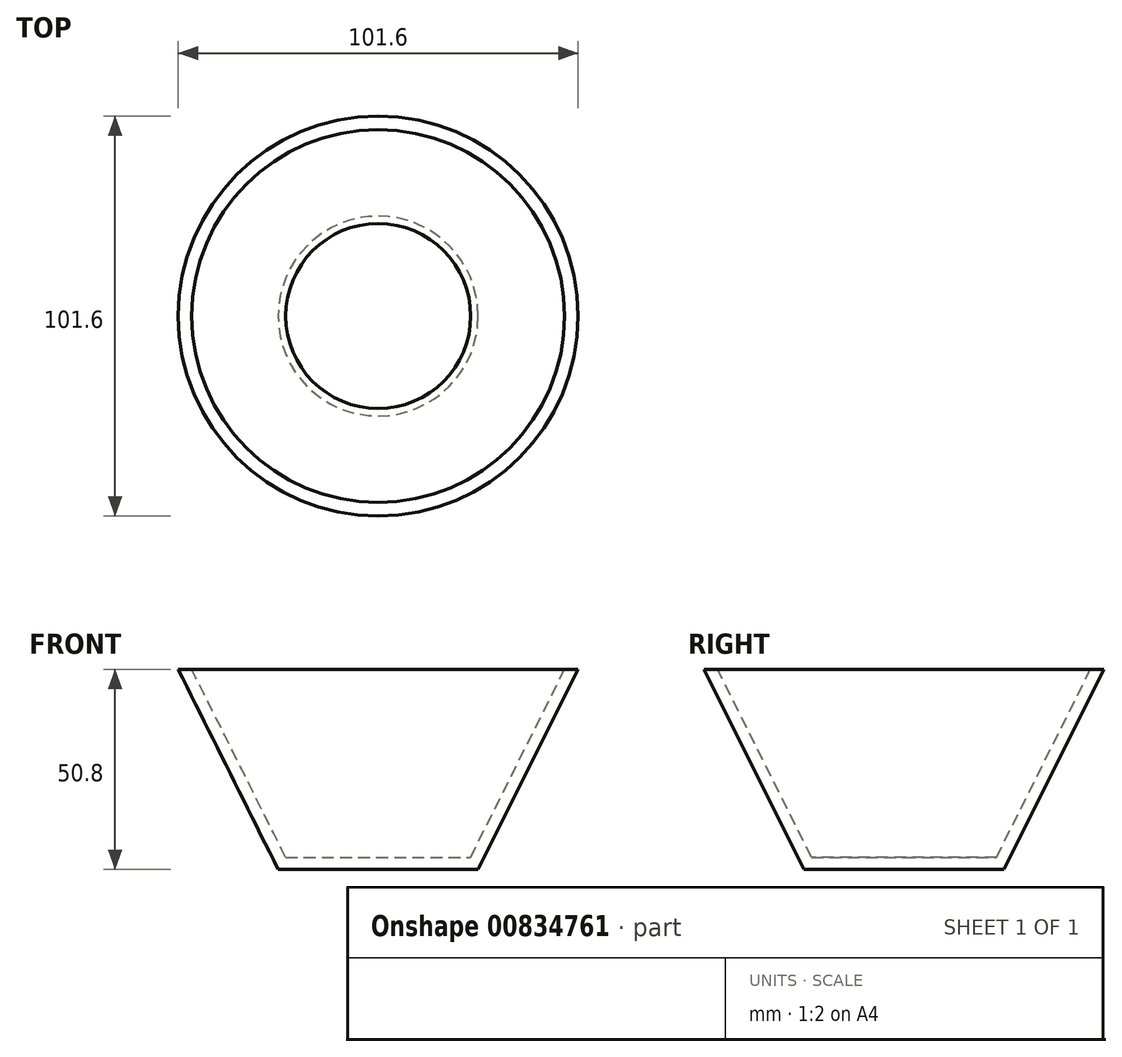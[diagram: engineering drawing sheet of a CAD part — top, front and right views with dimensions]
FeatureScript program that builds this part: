
annotation { "Feature Type Name" : "Feature", "Feature Type Description" : "" }
export const myFeature = defineFeature(function(context is Context, id is Id, definition is map)
    precondition{}
    {
        {
            var Q0;
            Q0=qCreatedBy(makeId("Front.planeOp"),FACE);
            var sketch = newSketch(context, id + "F0", { "sketchPlane" : qUnion([Q0])});
            skLineSegment(sketch, "E0", {"start": v(0, 0) * mm, "end": v(0, 50.8) * mm, "construction": true});
            skLineSegment(sketch, "E1", {"start": v(0, 0) * mm, "end": v(25.4, 0) * mm});
            skLineSegment(sketch, "E2", {"start": v(25.4, 0) * mm, "end": v(50.8, 50.8) * mm});
            skLineSegment(sketch, "E3.0", {"start": v(23.5, 3.07) * mm, "end": v(47.36, 50.8) * mm});
            skLineSegment(sketch, "E3.1", {"start": v(0, 3.07) * mm, "end": v(23.5, 3.07) * mm});
            skLineSegment(sketch, "E4", {"start": v(47.36, 50.8) * mm, "end": v(50.8, 50.8) * mm});
            skLineSegment(sketch, "E5", {"start": v(0, 3.07) * mm, "end": v(0, 0) * mm});
            skSolve(sketch);
        }
        {
            var Q0;
            Q0=makeQuery(id+"F0.imprint","IMPRINT",FACE,{"disambiguationData":[TD([[makeQuery(id+"F0.imprint","IMPRINT",EDGE,{"derivedFrom":sQuery(id+"F0.wireOp",EDGE,"E1")}),1.0]])]});
            var Q1;
            Q1=sQuery(id+"F0.wireOp",EDGE,"E0");
            revolve(context, id + "F1", {"surfaceOperationType" : NewSurfaceOperationType.NEW, "entities" : qUnion([Q0]), "axis" : qUnion([Q1]), "revolveType" : RevolveType.FULL});
        }
    });
